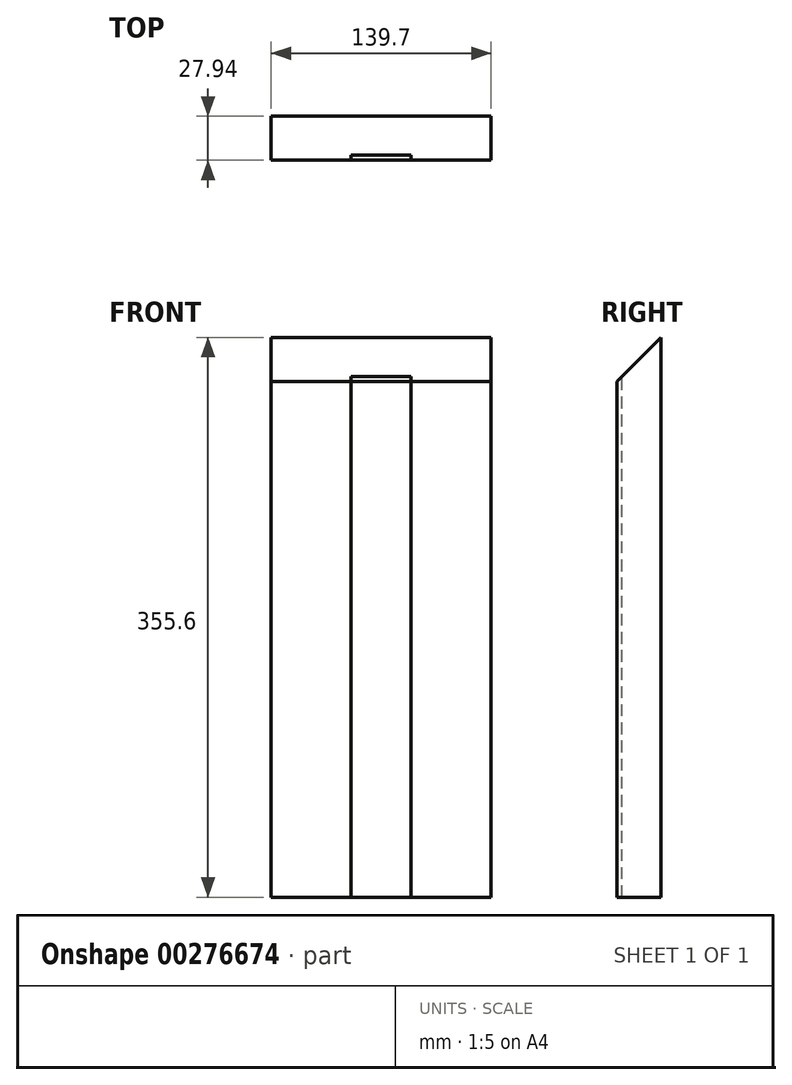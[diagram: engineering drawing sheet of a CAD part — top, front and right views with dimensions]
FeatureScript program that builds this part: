
annotation { "Feature Type Name" : "Feature", "Feature Type Description" : "" }
export const myFeature = defineFeature(function(context is Context, id is Id, definition is map)
    precondition{}
    {
        {
            var Q0;
            Q0=qCreatedBy(makeId("Top.planeOp"),FACE);
            var sketch = newSketch(context, id + "F0", { "sketchPlane" : qUnion([Q0])});
            skLineSegment(sketch, "E0.bottom", {"start": v(0, 0) * mm, "end": v(139.7, 0) * mm});
            skLineSegment(sketch, "E0.top", {"start": v(0, -27.94) * mm, "end": v(139.7, -27.94) * mm});
            skLineSegment(sketch, "E0.left", {"start": v(0, -27.94) * mm, "end": v(0, 0) * mm});
            skLineSegment(sketch, "E0.right", {"start": v(139.7, -27.94) * mm, "end": v(139.7, 0) * mm});
            skSolve(sketch);
        }
        {
            var Q0;
            Q0 = qSketchRegion(id + "F0", true);
            extrude(context, id + "F1", {"entities" : qUnion([Q0]), "depth" : 355.6 * mm});
        }
        {
            var Q0;
            Q0=makeQuery(id+"F1.opExtrude","CAP_EDGE",EDGE,{"disambiguationData":[OSD([sQuery(id+"F0.wireOp",EDGE,"E0.top")])],"isStart":false});
            chamfer(context, id + "F2", {"entities" : qUnion([Q0]), "width" : 27.94 * mm, "tangentPropagation" : true});
        }
        {
            var Q0;
            Q0=makeQuery(id+"F1.opExtrude","SWEPT_FACE",FACE,{"disambiguationData":[OSD([sQuery(id+"F0.wireOp",EDGE,"E0.top")])]});
            var sketch = newSketch(context, id + "F3", { "sketchPlane" : qUnion([Q0])});
            skLineSegment(sketch, "E1.bottom", {"start": v(50.8, 355.6) * mm, "end": v(88.9, 355.6) * mm});
            skLineSegment(sketch, "E1.top", {"start": v(50.8, 0) * mm, "end": v(88.9, 0) * mm});
            skLineSegment(sketch, "E1.left", {"start": v(50.8, 355.6) * mm, "end": v(50.8, 0) * mm});
            skLineSegment(sketch, "E1.right", {"start": v(88.9, 355.6) * mm, "end": v(88.9, 0) * mm});
            skSolve(sketch);
        }
        {
            var Q0;
            Q0 = qSketchRegion(id + "F3", true);
            extrude(context, id + "F4", {"entities" : qUnion([Q0]), "operationType" : NewBodyOperationType.REMOVE, "oppositeDirection" : true, "depth" : 3.17 * mm});
        }
        {
            var Q0;
            Q0=makeQuery(id+"F4.boolean.opBoolean","COPY",FACE,{"derivedFrom":makeQuery(id+"F4.opExtrude","SWEPT_FACE",FACE,{"disambiguationData":[OSD([sQuery(id+"F3.wireOp",EDGE,"E1.left")])]})});
            extrude(context, id + "F5", {"entities" : qUnion([Q0]), "endBound" : BoundingType.UP_TO_NEXT, "depth" : 25.4 * mm});
        }
    });
